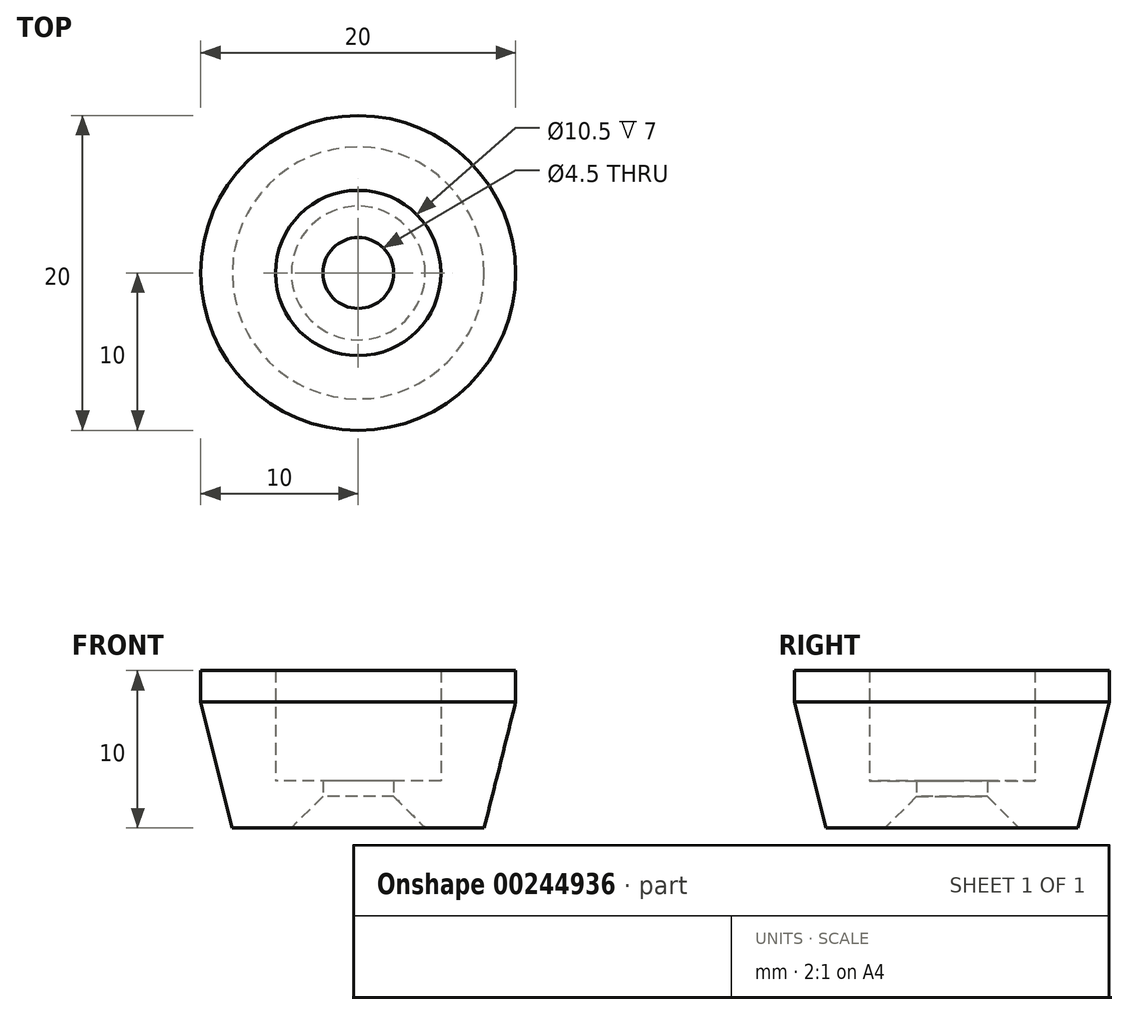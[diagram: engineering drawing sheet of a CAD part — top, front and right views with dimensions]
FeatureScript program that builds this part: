
annotation { "Feature Type Name" : "Feature", "Feature Type Description" : "" }
export const myFeature = defineFeature(function(context is Context, id is Id, definition is map)
    precondition{}
    {
        {
            var Q0;
            Q0=qCreatedBy(makeId("Top.planeOp"),FACE);
            var sketch = newSketch(context, id + "F0", { "sketchPlane" : qUnion([Q0])});
            skCircle(sketch, "E0", {"center": v(0, 0) * mm, "radius": 5.25 * mm});
            skCircle(sketch, "E1", {"center": v(0, 0) * mm, "radius": 10 * mm});
            skSolve(sketch);
        }
        {
            var Q0;
            Q0 = qSketchRegion(id + "F0", true);
            extrude(context, id + "F1", {"entities" : qUnion([Q0]), "depth" : 10 * mm});
        }
        {
            var Q0;
            Q0=qCreatedBy(makeId("Top.planeOp"),FACE);
            var sketch = newSketch(context, id + "F2", { "sketchPlane" : qUnion([Q0])});
            skCircle(sketch, "E2", {"center": v(0, 0) * mm, "radius": 5.25 * mm});
            skCircle(sketch, "E3", {"center": v(0, 0) * mm, "radius": 2.25 * mm});
            skSolve(sketch);
        }
        {
            var Q0;
            Q0 = qSketchRegion(id + "F2", true);
            extrude(context, id + "F3", {"entities" : qUnion([Q0]), "operationType" : NewBodyOperationType.ADD, "depth" : 3 * mm});
        }
        {
            var Q0;
            Q0=makeQuery(id+"F3.opExtrude","CAP_EDGE",EDGE,{"disambiguationData":[OSD([sQuery(id+"F2.wireOp",EDGE,"E3")])],"isStart":true});
            chamfer(context, id + "F4", {"entities" : qUnion([Q0]), "width" : 2 * mm, "tangentPropagation" : true});
        }
        {
            var Q0;
            Q0=makeQuery(id+"F1.opExtrude","CAP_EDGE",EDGE,{"disambiguationData":[OSD([sQuery(id+"F0.wireOp",EDGE,"E1")])],"isStart":true});
            chamfer(context, id + "F5", {"entities" : qUnion([Q0]), "chamferType" : ChamferType.TWO_OFFSETS, "width1" : 8 * mm, "oppositeDirection" : false, "width2" : 2 * mm, "tangentPropagation" : true});
        }
    });
